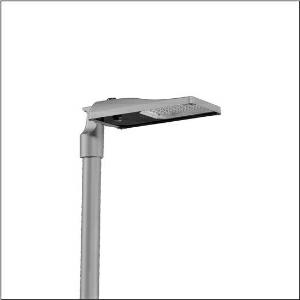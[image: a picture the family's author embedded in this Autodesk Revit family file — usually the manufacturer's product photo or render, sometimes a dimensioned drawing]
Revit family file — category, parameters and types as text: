
# Revit family: streetlight_sl_31_mini___st0_5a_5xh6b31t08ha_d023
name_source: partatom
category: Lighting Fixtures
units: mm (PartAtom-declared; Revit-internal decimal feet)

## family parameters
Cut with Voids When Loaded = No
Host = Face
Light Source = No
Part Type = Normal
Room Calculation Point = No
Round Connector Dimension = Use Diameter
Shared = No

## types (1)
- --- (1 x LED, 9230 lm, 68.3 W, 3000K)
    Apparent Load = 68 VA
    CIE Flux Codes = 41 75 97 100 100
    Color Rendering = 70
    Color Temperature = 3000K
    Default Elevation = 1800 mm
    Description = Streetlight SL 31 mini D4i, Desk-Remote mast luminaire for post-top, side-entry; light control with lens of PMMA; light distribution: ST0.5a, direct asymmetric distribution, for standard-compliant lighting for roads and squares; LED: luminous flux: 9.230lm, light colour: 730, colour temperature: 3000K; luminous efficacy: 135,1lm/W; control: pre-setting: logarithmic dimming characteristic, flexible luminous flux parameterisation, time-dependent luminous flux control, constant luminous flux control, power reduction, intelligent temperature release in ECG and LED module, overheat protection; luminaire housing, of diecast aluminium, Siteco® metallic grey (DB 702S), corrosivity category C5 high according to DIN EN ISO 12944; cover of toughened safety glass, transparent, opened without tools; mast flange of diecast aluminium, Siteco® metallic grey (DB 702S), spigot size: 76/60mm, mast flange included unmounted; with cable H07RN-F 2x 1.5mm², cable length: 8,5m, connection cable pre-assembled; mains connection: 220..240V, AC, 50/60Hz; power consumption (at start of service life): 68,3W / (at end of service life): 74,5W / (with reduced operation 50%): 29,5W; protection rating (complete): IP66; insulation class (complete): insulation class II (safety insulation); impact resistance: IK09; certification: CE, ENEC, ENEC+, VDE, UKCA, ZD4i; permissible operating ambient temperature for outdoor applications: -40..+50°C; packaging unit: 1 piece

Light Distribution: ST0.5a
    Height = 76 mm
    Lamp = 1 x LED
    Lamp Light Flux = 9230 lm
    Lamp Power = 68.3 W
    Lamp count = 1
    Length = 547 mm
    Luminous efficacy = 135 lm/W
    Manufacturer = Siteco
    ModVariant = No
    Model = 5XH6B31T08HA
    Number of Poles = 1
    OnlyDefault = Yes
    Power Factor = 1
    Product Name = Streetlight SL 31 mini | ST0.5a
    Product group = mast luminaire | pylon top
    ProductGroupID = 6100
    Protection Class = Protection class II
    Protection Degree = IP 66
    RLX_Detail_Level = 1
    RLX_Emergency_Light_Flux = 0 lm
    RLX_Emergency_Type = 0
    RLX_Emergency_Type_DB = No
    RlxData = <blob elided: 35341 chars, md5=ab02a0b3>
    Socket = socket
    Standby Power = 0 W
    System Light Flux = 9230 lm
    System Power = 68 W
    Type Comments = factory setting: luminous flux: 100 % | dim-lin: 254 | 692 mA
    Type Image = l_1300332.jpg
    URL = http://relux.com
    VarID = @adj_002477
    Voltage = 0 V
    Weight = 0.00 kg
    Width = 265 mm

## geometry (parser evidence)
native form markers: Blend x4, Sweep x11
no freeform markers — native parametric forms only
